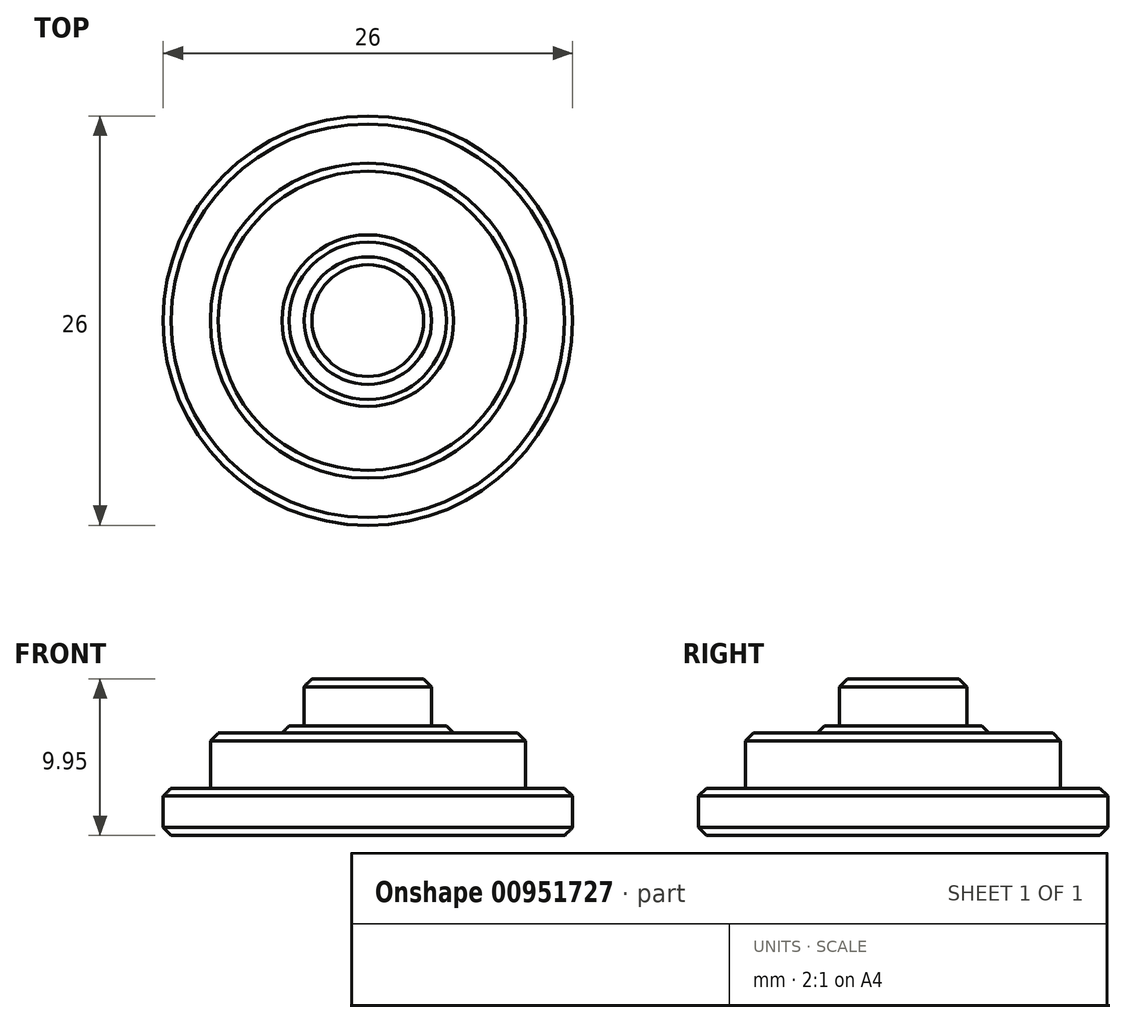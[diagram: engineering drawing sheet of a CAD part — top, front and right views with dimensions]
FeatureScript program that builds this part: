
annotation { "Feature Type Name" : "Feature", "Feature Type Description" : "" }
export const myFeature = defineFeature(function(context is Context, id is Id, definition is map)
    precondition{}
    {
        {
            var Q0;
            Q0=qCreatedBy(makeId("Front.planeOp"),FACE);
            var sketch = newSketch(context, id + "F0", { "sketchPlane" : qUnion([Q0])});
            skLineSegment(sketch, "E0", {"start": v(0, 0) * mm, "end": v(13, 0) * mm});
            skLineSegment(sketch, "E1", {"start": v(13, 0) * mm, "end": v(13, 3) * mm});
            skLineSegment(sketch, "E2", {"start": v(13, 3) * mm, "end": v(10, 3) * mm});
            skLineSegment(sketch, "E3", {"start": v(10, 3) * mm, "end": v(10, 6.5) * mm});
            skLineSegment(sketch, "E4", {"start": v(4.05, 9.95) * mm, "end": v(0, 9.95) * mm});
            skLineSegment(sketch, "E5", {"start": v(0, 9.95) * mm, "end": v(0, 0) * mm});
            skLineSegment(sketch, "E6", {"start": v(10, 6.5) * mm, "end": v(5.5, 6.5) * mm});
            skLineSegment(sketch, "E7", {"start": v(5.5, 6.5) * mm, "end": v(5.5, 6.95) * mm});
            skLineSegment(sketch, "E8", {"start": v(5.5, 6.95) * mm, "end": v(4.05, 6.95) * mm});
            skLineSegment(sketch, "E9", {"start": v(4.05, 6.95) * mm, "end": v(4.05, 9.95) * mm});
            skSolve(sketch);
        }
        {
            var Q0;
            Q0=makeQuery(id+"F0.imprint","IMPRINT",FACE,{"disambiguationData":[TD([[makeQuery(id+"F0.imprint","IMPRINT",EDGE,{"derivedFrom":sQuery(id+"F0.wireOp",EDGE,"E0")}),1.0]])]});
            var Q1;
            Q1=sQuery(id+"F0.wireOp",EDGE,"E5");
            revolve(context, id + "F1", {"surfaceOperationType" : NewSurfaceOperationType.NEW, "entities" : qUnion([Q0]), "axis" : qUnion([Q1]), "revolveType" : RevolveType.FULL});
        }
        {
            var Q0;
            Q0=makeQuery(id+"F1.opRevolve","SWEPT_EDGE",EDGE,{"disambiguationData":[OSD([sQuery(id+"F0.wireOp",EDGE,"E0"),sQuery(id+"F0.wireOp",EDGE,"E1")])]});
            var Q1;
            Q1=makeQuery(id+"F1.opRevolve","SWEPT_EDGE",EDGE,{"disambiguationData":[OSD([sQuery(id+"F0.wireOp",EDGE,"E1"),sQuery(id+"F0.wireOp",EDGE,"E2")])]});
            var Q2;
            Q2=makeQuery(id+"F1.opRevolve","SWEPT_EDGE",EDGE,{"disambiguationData":[OSD([sQuery(id+"F0.wireOp",EDGE,"E3"),sQuery(id+"F0.wireOp",EDGE,"E6")])]});
            var Q3;
            Q3=makeQuery(id+"F1.opRevolve","SWEPT_EDGE",EDGE,{"disambiguationData":[OSD([sQuery(id+"F0.wireOp",EDGE,"E7"),sQuery(id+"F0.wireOp",EDGE,"E8")])]});
            var Q4;
            Q4=makeQuery(id+"F1.opRevolve","SWEPT_EDGE",EDGE,{"disambiguationData":[OSD([sQuery(id+"F0.wireOp",EDGE,"E4"),sQuery(id+"F0.wireOp",EDGE,"E9")])]});
            chamfer(context, id + "F2", {"entities" : qUnion([Q0, Q1, Q2, Q3, Q4]), "width" : 0.5 * mm, "tangentPropagation" : true});
        }
    });
